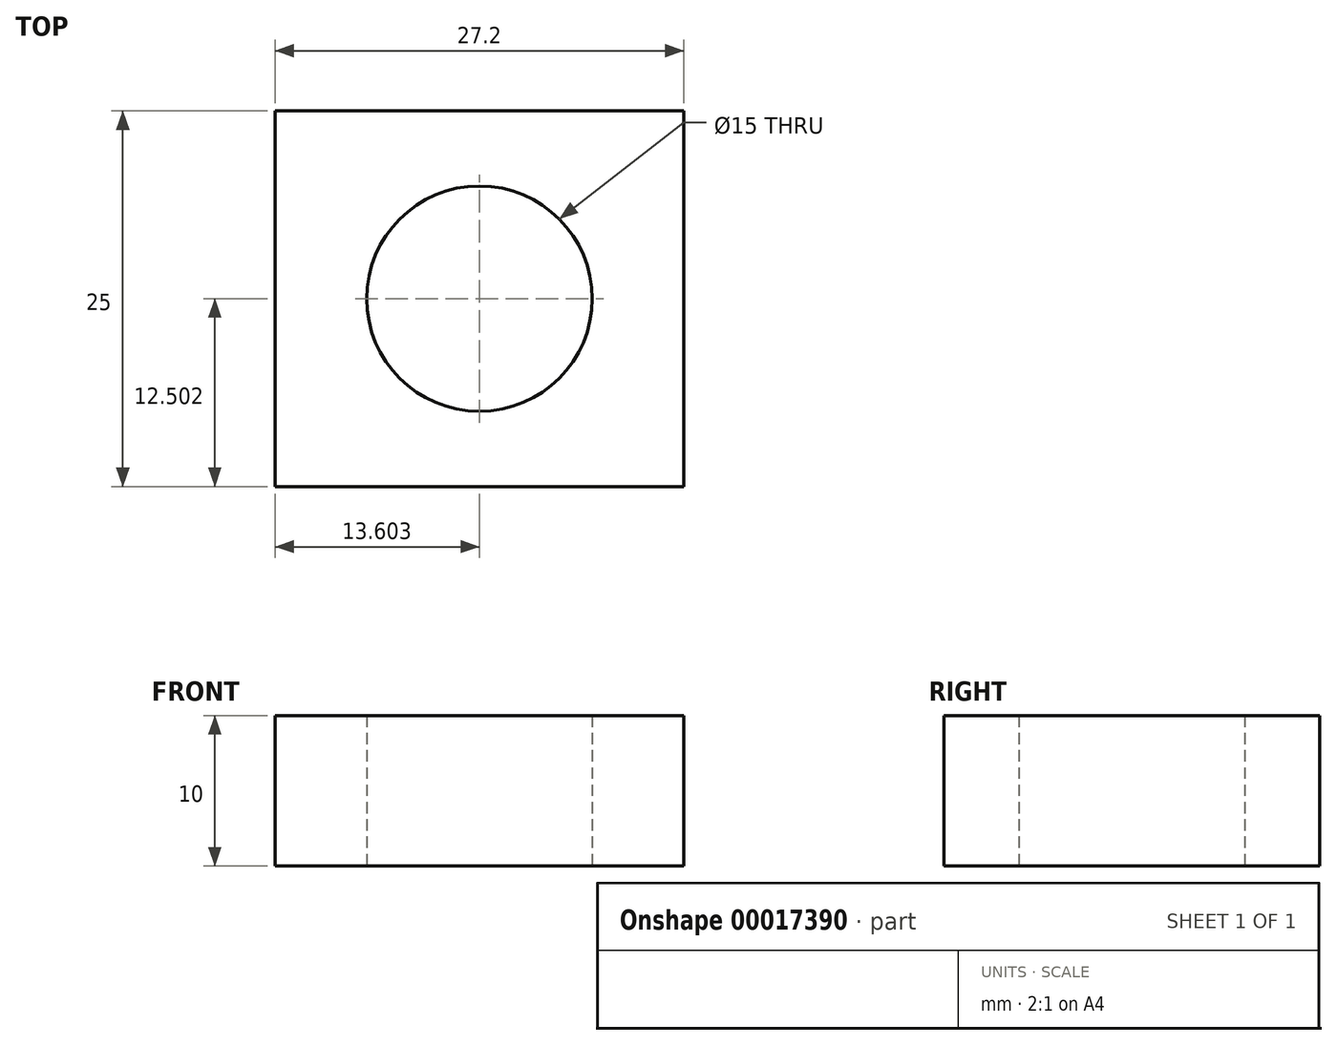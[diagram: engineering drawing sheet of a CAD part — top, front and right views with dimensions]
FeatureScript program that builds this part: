
annotation { "Feature Type Name" : "Feature", "Feature Type Description" : "" }
export const myFeature = defineFeature(function(context is Context, id is Id, definition is map)
    precondition{}
    {
        {
            var Q0;
            Q0=qCreatedBy(makeId("Top.planeOp"),FACE);
            var sketch = newSketch(context, id + "F0", { "sketchPlane" : qUnion([Q0])});
            skLineSegment(sketch, "E0.bottom", {"start": v(-12.6, 13.6) * mm, "end": v(14.6, 13.6) * mm});
            skLineSegment(sketch, "E0.top", {"start": v(-12.6, -11.4) * mm, "end": v(14.6, -11.4) * mm});
            skLineSegment(sketch, "E0.left", {"start": v(-12.6, 13.6) * mm, "end": v(-12.6, -11.4) * mm});
            skLineSegment(sketch, "E0.right", {"start": v(14.6, 13.6) * mm, "end": v(14.6, -11.4) * mm});
            skCircle(sketch, "E1", {"center": v(1, 1.1) * mm, "radius": 7.5 * mm});
            skSolve(sketch);
        }
        {
            var Q0;
            Q0 = qSketchRegion(id + "F0", true);
            extrude(context, id + "F1", {"entities" : qUnion([Q0]), "depth" : 10 * mm});
        }
    });
